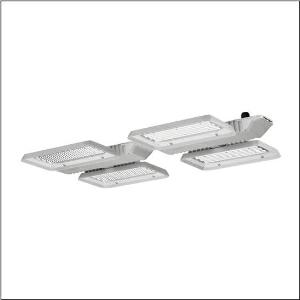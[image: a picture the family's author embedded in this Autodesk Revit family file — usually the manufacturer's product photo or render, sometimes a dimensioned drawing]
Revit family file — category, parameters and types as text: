
# Revit family: highbay_11_51hla1d24nca
name_source: partatom
category: Lighting Fixtures
units: mm (PartAtom-declared; Revit-internal decimal feet)

## family parameters
Cut with Voids When Loaded = No
Host = Face
Light Source = No
Part Type = Normal
Room Calculation Point = No
Round Connector Dimension = Use Diameter
Shared = No

## types (1)
- --- (1 x LED, 32370 lm, 189.6 W, 4000K)
    Apparent Load = 190 VA
    CIE Flux Codes = 88 95 99 100 99
    Color Rendering = 80
    Color Temperature = 4000K
    Default Elevation = 1800 mm
    Description = Highbay 11, LED high bay luminaire, primary light control with lens, of PMMA, light emission: direct distribution, primary light characteristic: symmetric, installation type: suspended mounting, surface-mounted, for 2x 2x LED, rated luminous flux: 32.370lm, luminous efficacy: 171lm/W, light colour: 840, colour temperature: 4000K, control gear: ECG DALI, with terminal, 5-pole, max. 2.5mm², mains connection: 230..240V, AC, 50/60Hz, rated input power: 190W, LED unit, of diecast aluminium, unplated, bead blasted, silver, length: 940mm, width: 500mm, height: 65mm, housing, of diecast aluminium, uncoated, bead blasted, silver, protection rating (complete): IP65, insulation class (complete): insulation class I (protective earthing), certification: CE, ENEC, VDE, UKCA, protection symbol: D, impact resistance: IK08 with glass or PC cover, permissible operating ambient temperature: -35..+45°C, reducing of maximum allowable ambient temperature of 5°C with ceiling mounting, corresponds to IFS (International Featured Standards) requirements for safety and quality in the food industry, packaging unit: 1 piece
    Height = 95 mm
    Lamp = 1 x LED
    Lamp Light Flux = 32370 lm
    Lamp Power = 189.6 W
    Lamp count = 1
    Length = 939 mm
    Luminous efficacy = 171 lm/W
    Manufacturer = Siteco
    ModVariant = No
    Model = 51HLA1D24NCA
    Mounting Place = Ceiling
    Mounting Type = Pendant
    Number of Poles = 1
    OnlyDefault = Yes
    Power Factor = 1
    Product Name = Highbay 11
    Product group = LED high bay luminaire
    ProductGroupID = 903
    Protection Class = Protection class I
    Protection Degree = IP 65
    RLX_Detail_Level = 1
    RLX_Emergency_Light_Flux = 0 lm
    RLX_Emergency_Type = 0
    RLX_Emergency_Type_DB = No
    RlxData = <blob elided: 100245 chars, md5=3a5095e0>
    Socket = socket
    Standby Power = 0 W
    System Light Flux = 32370 lm
    System Power = 190 W
    Type Comments = factory setting: luminous flux: 100 % | dim-lin: 254 | 535 mA
    Type Image = l_1003428.jpg
    URL = http://relux.com
    VarID = @adj_177591
    Voltage = 0 V
    Weight = 0.00 kg
    Width = 501 mm

## geometry (parser evidence)
native form markers: Blend x4, Sweep x13
no freeform markers — native parametric forms only
